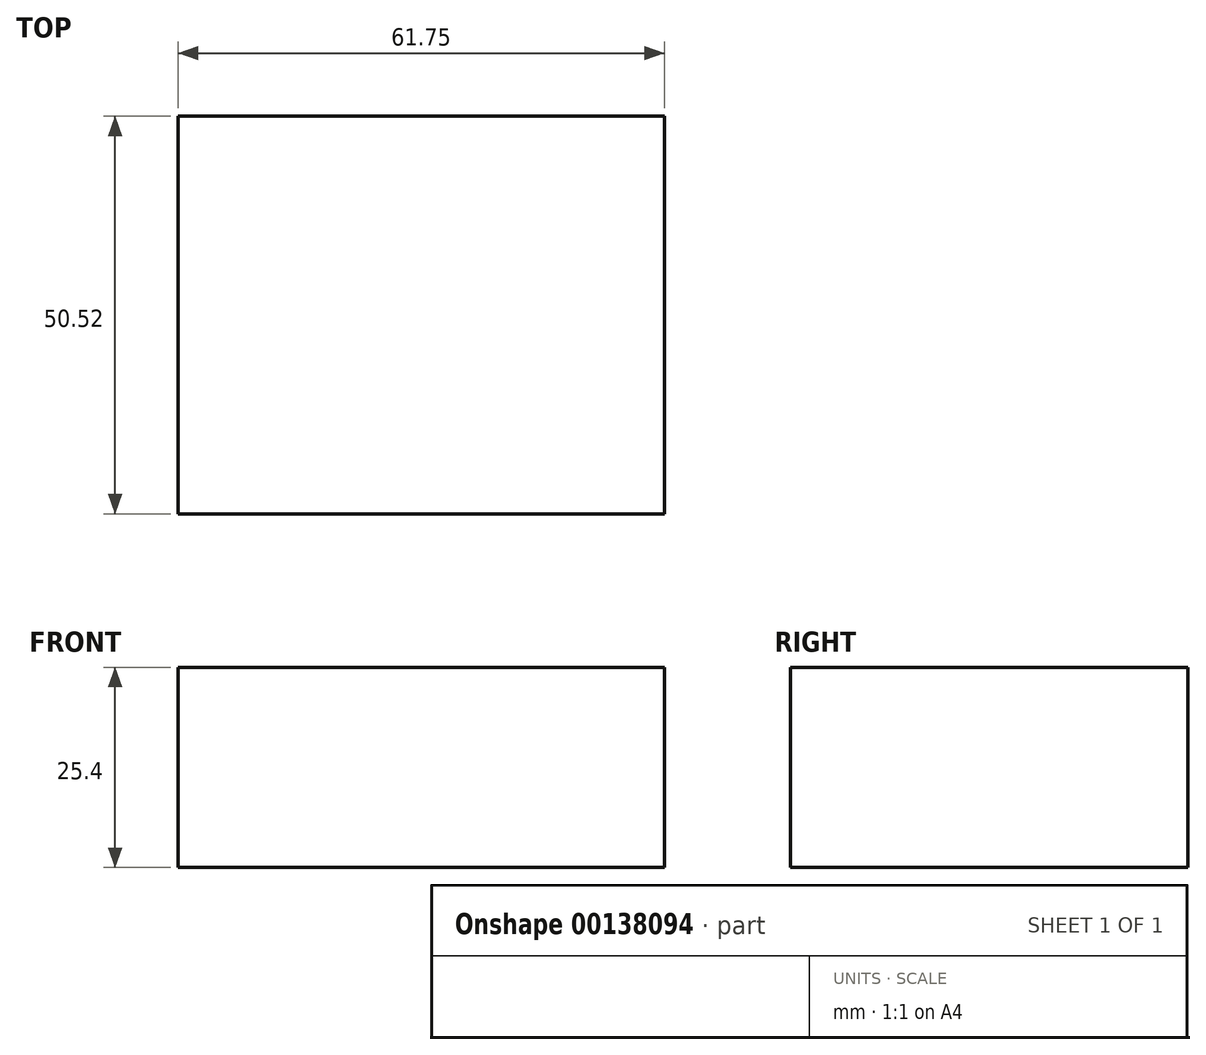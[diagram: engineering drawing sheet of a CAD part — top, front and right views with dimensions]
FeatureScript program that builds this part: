
annotation { "Feature Type Name" : "Feature", "Feature Type Description" : "" }
export const myFeature = defineFeature(function(context is Context, id is Id, definition is map)
    precondition{}
    {
        {
            var Q0;
            Q0=qCreatedBy(makeId("Top.planeOp"),FACE);
            var sketch = newSketch(context, id + "F0", { "sketchPlane" : qUnion([Q0])});
            skLineSegment(sketch, "E0.bottom", {"start": v(-31.3, 24.18) * mm, "end": v(30.44, 24.18) * mm});
            skLineSegment(sketch, "E0.top", {"start": v(-31.3, -26.34) * mm, "end": v(30.44, -26.34) * mm});
            skLineSegment(sketch, "E0.left", {"start": v(-31.3, 24.18) * mm, "end": v(-31.3, -26.34) * mm});
            skLineSegment(sketch, "E0.right", {"start": v(30.44, 24.18) * mm, "end": v(30.44, -26.34) * mm});
            skSolve(sketch);
        }
        {
            var Q0;
            Q0 = qSketchRegion(id + "F0", true);
            extrude(context, id + "F1", {"entities" : qUnion([Q0]), "depth" : 25.4 * mm});
        }
    });
